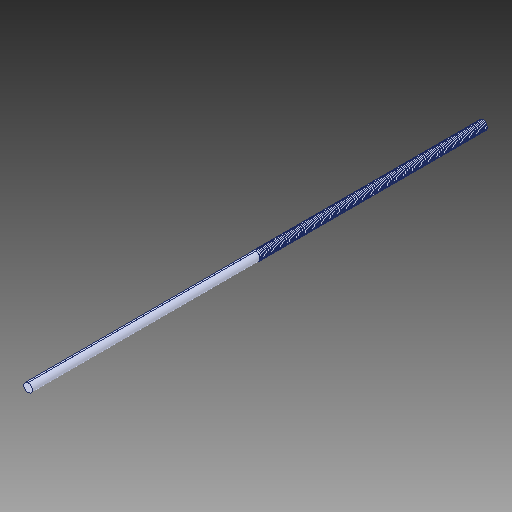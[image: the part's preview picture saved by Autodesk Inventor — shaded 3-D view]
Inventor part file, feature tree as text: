
AUTODESK INVENTOR PART (.ipt)
format: ipt  version: 2019 (Build 230136000, 136)  size: 2,196,480 bytes
history: native  units: in
note: dims shown in document units (in); Inventor stores cm internally (conversion verified against a paired STEP export)
features: other x3, sketch x1
ambient origin geometry x8: Origin, YZ Plane, XZ Plane, XY Plane, X Axis, Y Axis, Z Axis, Center Point
bodies: Solid1 (feature_tree)
feature tree (4):
  other  "LeadScrew.ipt"
  other  "Solid1::LeadScrew.ipt"
  other  "TaggingFeature1"
  sketch  "Sketch1"  dims[d0=0.3937in]
